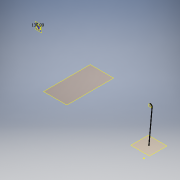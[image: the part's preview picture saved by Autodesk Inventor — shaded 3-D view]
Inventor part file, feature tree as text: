
AUTODESK INVENTOR PART (.ipt)
format: ipt  version: 2017 (Build 210142000, 142)  size: 158,208 bytes
history: native  units: mm
features: plane x3, other x3, sketch x2, sweep x1, reference x1
ambient origin geometry x8: Origin, YZ Plane, XZ Plane, XY Plane, X Axis, Y Axis, Z Axis, Center Point
bodies: Body1 (feature_tree)
feature tree (10):
  plane  "Work Plane3"
  plane  "Work Plane7"
  plane  "Work Plane2"
  sweep  "Sweep3"
  sketch  "3D Sketch1"
  sketch  "Sketch2"  dims[d0=8.0mm d6=0.0mm d7=0.0mm]
  reference  "Reference1"
  other  "<userpath>\OneDrive\Inventor\VolledigGeassembleerdv001.iam"
  other  "VolledigGeassembleerdv001.iam"
  other  "winch:1"
